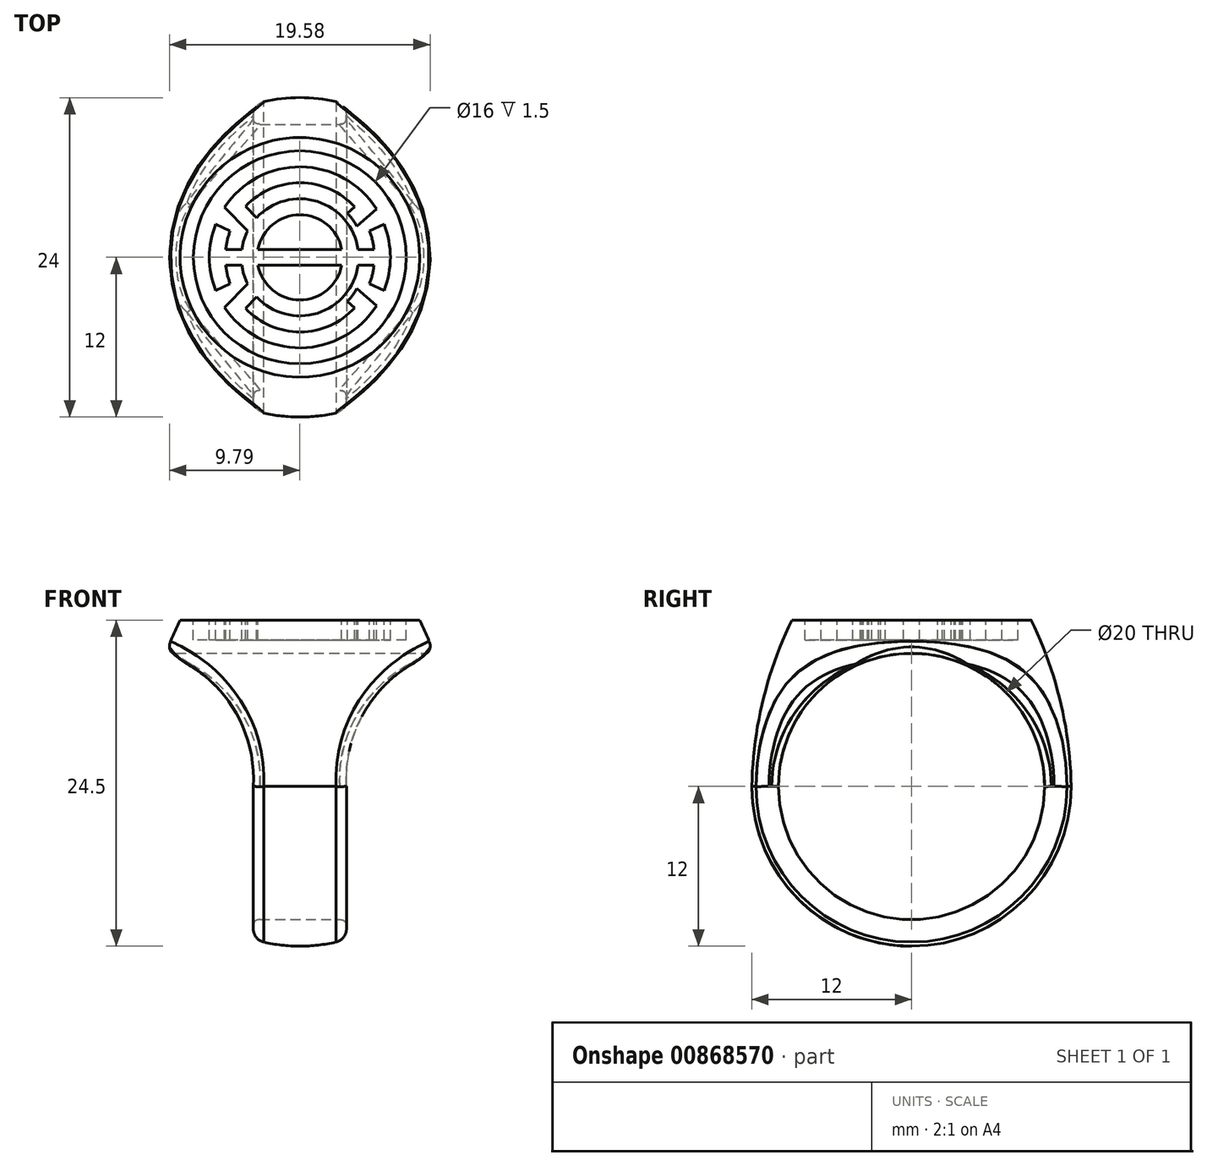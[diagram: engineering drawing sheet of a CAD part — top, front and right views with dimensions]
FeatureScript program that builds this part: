
annotation { "Feature Type Name" : "Feature", "Feature Type Description" : "" }
export const myFeature = defineFeature(function(context is Context, id is Id, definition is map)
    precondition{}
    {
        {
            var Q0;
            Q0=qCreatedBy(makeId("Right.planeOp"),FACE);
            var sketch = newSketch(context, id + "F0", { "sketchPlane" : qUnion([Q0])});
            skLineSegment(sketch, "E0", {"start": v(0, 0) * mm, "end": v(0, -24.5) * mm});
            skLineSegment(sketch, "E1", {"start": v(0, 0) * mm, "end": v(-9, 0) * mm});
            skArc(sketch, "E2", {"start": v(-12, -12.5) * mm, "mid": v(-8.49, -20.99) * mm, "end": v(0, -24.5) * mm});
            skLineSegment(sketch, "E3", {"start": v(0, -12.5) * mm, "end": v(-12, -12.5) * mm, "construction": true});
            skArc(sketch, "E4", {"start": v(-9, 0) * mm, "mid": v(-11.18, -6.09) * mm, "end": v(-12, -12.5) * mm});
            skSolve(sketch);
        }
        {
            var Q0;
            Q0=makeQuery(id+"F0.imprint","IMPRINT",FACE,{"disambiguationData":[TD([[makeQuery(id+"F0.imprint","IMPRINT",EDGE,{"derivedFrom":sQuery(id+"F0.wireOp",EDGE,"E0")}),-1.0]])]});
            var Q1;
            Q1=sQuery(id+"F0.wireOp",EDGE,"E0");
            revolve(context, id + "F1", {"entities" : qUnion([Q0]), "axis" : qUnion([Q1]), "revolveType" : RevolveType.FULL});
        }
        {
            var Q0;
            Q0=qCreatedBy(makeId("Right.planeOp"),FACE);
            var sketch = newSketch(context, id + "F2", { "sketchPlane" : qUnion([Q0])});
            skCircle(sketch, "E5", {"center": v(0, -12.5) * mm, "radius": 10 * mm});
            skSolve(sketch);
        }
        {
            var Q0;
            Q0=qSketchRegion(id+"F2",true);
            extrude(context, id + "F3", {"entities" : qUnion([Q0]), "operationType" : NewBodyOperationType.REMOVE, "endBound" : BoundingType.SYMMETRIC, "oppositeDirection" : true, "depth" : 25 * mm, "offsetDistance" : 25 * mm});
        }
        {
            var Q0;
            Q0=qCreatedBy(makeId("Front.planeOp"),FACE);
            var sketch = newSketch(context, id + "F4", { "sketchPlane" : qUnion([Q0])});
            skLineSegment(sketch, "E6", {"start": v(3.5, -26.5) * mm, "end": v(3.5, -12.5) * mm});
            skArc(sketch, "E7", {"start": v(10.15, -2.5) * mm, "mid": v(5.16, -6.39) * mm, "end": v(3.5, -12.5) * mm});
            skLineSegment(sketch, "E8", {"start": v(10.15, -2.5) * mm, "end": v(11.65, -2.5) * mm});
            skLineSegment(sketch, "E9", {"start": v(11.65, -2.5) * mm, "end": v(11.65, -26.5) * mm});
            skLineSegment(sketch, "E10", {"start": v(11.65, -26.5) * mm, "end": v(3.5, -26.5) * mm});
            skPoint(sketch, "E11.start.orphan", {"position": v(0, -24.5) * mm});
            skLineSegment(sketch, "E12", {"start": v(0, 0) * mm, "end": v(0, -24.5) * mm, "construction": true});
            skLineSegment(sketch, "E13.MirrorCS", {"start": v(-3.5, -26.5) * mm, "end": v(-3.5, -12.5) * mm});
            skArc(sketch, "E14.MirrorCS", {"start": v(-10.15, -2.5) * mm, "mid": v(-5.16, -6.39) * mm, "end": v(-3.5, -12.5) * mm});
            skLineSegment(sketch, "E15.MirrorCS", {"start": v(-11.65, -2.5) * mm, "end": v(-11.65, -26.5) * mm});
            skLineSegment(sketch, "E16.MirrorCS", {"start": v(-11.65, -26.5) * mm, "end": v(-3.5, -26.5) * mm});
            skLineSegment(sketch, "E17.MirrorCS", {"start": v(-10.15, -2.5) * mm, "end": v(-11.65, -2.5) * mm});
            skSolve(sketch);
        }
        {
            var Q0;
            Q0=qSketchRegion(id+"F4",true);
            extrude(context, id + "F5", {"entities" : qUnion([Q0]), "operationType" : NewBodyOperationType.REMOVE, "endBound" : BoundingType.SYMMETRIC, "depth" : 25 * mm, "offsetDistance" : 25 * mm});
        }
        {
            var Q0;
            Q0=makeQuery(id+"F1.opRevolve","SWEPT_FACE",FACE,{"disambiguationData":[OSD([sQuery(id+"F0.wireOp",EDGE,"E1")])]});
            var sketch = newSketch(context, id + "F6", { "sketchPlane" : qUnion([Q0])});
            skCircle(sketch, "E18", {"center": v(0, 0) * mm, "radius": 8 * mm});
            skLineSegment(sketch, "E19", {"start": v(-8, 0) * mm, "end": v(8, 0) * mm, "construction": true});
            skArc(sketch, "E20", {"start": v(3.14, 0.6) * mm, "mid": v(0, 3.2) * mm, "end": v(-3.14, 0.6) * mm});
            skArc(sketch, "E21", {"start": v(4.36, 0.6) * mm, "mid": v(1.32, 4.2) * mm, "end": v(-3.24, 2.98) * mm});
            skArc(sketch, "E22", {"start": v(5.57, 0.6) * mm, "mid": v(5.45, 1.3) * mm, "end": v(5.24, 1.98) * mm});
            skArc(sketch, "E23", {"start": v(6.8, 0) * mm, "mid": v(6.68, 1.26) * mm, "end": v(6.33, 2.49) * mm});
            skLineSegment(sketch, "E24", {"start": v(-4.08, 3.84) * mm, "end": v(-3.24, 2.98) * mm});
            skLineSegment(sketch, "E25", {"start": v(-5.67, 3.75) * mm, "end": v(-3.93, 1.98) * mm});
            skLineSegment(sketch, "E26", {"start": v(-6.33, 2.49) * mm, "end": v(-5.24, 1.98) * mm});
            skArc(sketch, "E27.trimOffspring", {"start": v(-6.33, 2.49) * mm, "mid": v(-6.68, 1.26) * mm, "end": v(-6.8, 0) * mm});
            skArc(sketch, "E28.trimOffspring", {"start": v(-5.24, 1.98) * mm, "mid": v(-5.45, 1.3) * mm, "end": v(-5.57, 0.6) * mm});
            skArc(sketch, "E29.trimOffspring", {"start": v(-3.93, 1.98) * mm, "mid": v(-4.2, 1.3) * mm, "end": v(-4.36, 0.6) * mm});
            skLineSegment(sketch, "E30", {"start": v(-5.57, 0.6) * mm, "end": v(-4.36, 0.6) * mm});
            skLineSegment(sketch, "E31", {"start": v(5.24, 1.98) * mm, "end": v(6.33, 2.49) * mm});
            skLineSegment(sketch, "E32", {"start": v(5.75, 3.62) * mm, "end": v(4.29, 2.33) * mm});
            skLineSegment(sketch, "E33", {"start": v(3.58, 3.3) * mm, "end": v(4.13, 3.79) * mm});
            skLineSegment(sketch, "E34.trimOffspring", {"start": v(4.36, 0.6) * mm, "end": v(5.57, 0.6) * mm});
            skPoint(sketch, "E35.orphan", {"position": v(4.4, 0) * mm});
            skPoint(sketch, "E36.orphan", {"position": v(5.6, 0) * mm});
            skArc(sketch, "E37.trimOffspring", {"start": v(4.13, 3.79) * mm, "mid": v(0.04, 5.6) * mm, "end": v(-4.08, 3.84) * mm});
            skArc(sketch, "E38.trimOffspring", {"start": v(5.75, 3.62) * mm, "mid": v(0.08, 6.8) * mm, "end": v(-5.67, 3.75) * mm});
            skPoint(sketch, "E39.orphan", {"position": v(-5.6, 0) * mm});
            skPoint(sketch, "E40.orphan", {"position": v(-4.4, 0) * mm});
            skLineSegment(sketch, "E41.trimOffspring", {"start": v(-3.14, 0.6) * mm, "end": v(3.14, 0.6) * mm});
            skPoint(sketch, "E42.orphan", {"position": v(-3.2, 0) * mm});
            skArc(sketch, "E43", {"start": v(4.29, 2.33) * mm, "mid": v(3.97, 2.84) * mm, "end": v(3.58, 3.3) * mm});
            skArc(sketch, "E44.MirrorCS", {"start": v(-6.33, -2.49) * mm, "mid": v(-6.68, -1.26) * mm, "end": v(-6.8, 0) * mm});
            skLineSegment(sketch, "E45.MirrorCS", {"start": v(-6.33, -2.49) * mm, "end": v(-5.24, -1.98) * mm});
            skArc(sketch, "E46.MirrorCS", {"start": v(-5.24, -1.98) * mm, "mid": v(-5.45, -1.3) * mm, "end": v(-5.57, -0.6) * mm});
            skLineSegment(sketch, "E47.MirrorCS", {"start": v(-5.57, -0.6) * mm, "end": v(-4.36, -0.6) * mm});
            skArc(sketch, "E48.MirrorCS", {"start": v(-3.93, -1.98) * mm, "mid": v(-4.2, -1.3) * mm, "end": v(-4.36, -0.6) * mm});
            skLineSegment(sketch, "E49.MirrorCS", {"start": v(-5.67, -3.75) * mm, "end": v(-3.93, -1.98) * mm});
            skArc(sketch, "E50.MirrorCS", {"start": v(5.75, -3.62) * mm, "mid": v(0.08, -6.8) * mm, "end": v(-5.67, -3.75) * mm});
            skLineSegment(sketch, "E51.MirrorCS", {"start": v(5.75, -3.62) * mm, "end": v(4.29, -2.33) * mm});
            skArc(sketch, "E52.MirrorCS", {"start": v(4.29, -2.33) * mm, "mid": v(3.97, -2.84) * mm, "end": v(3.58, -3.3) * mm});
            skArc(sketch, "E53.MirrorCS", {"start": v(4.13, -3.79) * mm, "mid": v(0.04, -5.6) * mm, "end": v(-4.08, -3.84) * mm});
            skLineSegment(sketch, "E54.MirrorCS", {"start": v(-4.08, -3.84) * mm, "end": v(-3.24, -2.98) * mm});
            skArc(sketch, "E55.MirrorCS", {"start": v(4.36, -0.6) * mm, "mid": v(1.32, -4.2) * mm, "end": v(-3.24, -2.98) * mm});
            skLineSegment(sketch, "E56.MirrorCS", {"start": v(4.36, -0.6) * mm, "end": v(5.57, -0.6) * mm});
            skArc(sketch, "E57.MirrorCS", {"start": v(5.57, -0.6) * mm, "mid": v(5.45, -1.3) * mm, "end": v(5.24, -1.98) * mm});
            skLineSegment(sketch, "E58.MirrorCS", {"start": v(5.24, -1.98) * mm, "end": v(6.33, -2.49) * mm});
            skArc(sketch, "E59.MirrorCS", {"start": v(6.8, 0) * mm, "mid": v(6.68, -1.26) * mm, "end": v(6.33, -2.49) * mm});
            skLineSegment(sketch, "E60.MirrorCS", {"start": v(-3.14, -0.6) * mm, "end": v(3.14, -0.6) * mm});
            skArc(sketch, "E61.MirrorCS", {"start": v(3.14, -0.6) * mm, "mid": v(0, -3.2) * mm, "end": v(-3.14, -0.6) * mm});
            skLineSegment(sketch, "E62.MirrorCS", {"start": v(3.58, -3.3) * mm, "end": v(4.13, -3.79) * mm});
            skSolve(sketch);
        }
        {
            var Q0;
            Q0=makeQuery(id+"F6.imprint","IMPRINT",FACE,{"disambiguationData":[TD([[makeQuery(id+"F6.imprint","IMPRINT",EDGE,{"derivedFrom":sQuery(id+"F6.wireOp",EDGE,"E18")}),1.0]])]});
            var Q1;
            Q1=makeQuery(id+"F6.imprint","IMPRINT",FACE,{"disambiguationData":[TD([[makeQuery(id+"F6.imprint","IMPRINT",EDGE,{"derivedFrom":sQuery(id+"F6.wireOp",EDGE,"E20")}),1.0]])]});
            var Q2;
            Q2=makeQuery(id+"F6.imprint","IMPRINT",FACE,{"disambiguationData":[TD([[makeQuery(id+"F6.imprint","IMPRINT",EDGE,{"derivedFrom":sQuery(id+"F6.wireOp",EDGE,"E60.MirrorCS")}),-1.0]])]});
            extrude(context, id + "F7", {"entities" : qUnion([Q0, Q1, Q2]), "operationType" : NewBodyOperationType.REMOVE, "oppositeDirection" : true, "depth" : 1.5 * mm, "offsetDistance" : 25 * mm});
        }
        {
            var Q0;
            Q0=makeQuery(id+"F5.boolean.opBoolean","INTERSECT",EDGE,{"disambiguationData":[OD(1.0)],"derivedFrom":[makeQuery(id+"F1.opRevolve","SWEPT_FACE",FACE,{"disambiguationData":[OSD([sQuery(id+"F0.wireOp",EDGE,"E4")])]}),makeQuery(id+"F5.opExtrude","SWEPT_FACE",FACE,{"disambiguationData":[OSD([sQuery(id+"F4.wireOp",EDGE,"E14.MirrorCS")])]})]});
            var Q1;
            Q1=makeQuery(id+"F5.boolean.opBoolean","INTERSECT",EDGE,{"derivedFrom":[makeQuery(id+"F1.opRevolve","SWEPT_FACE",FACE,{"disambiguationData":[OSD([sQuery(id+"F0.wireOp",EDGE,"E2")])]}),makeQuery(id+"F5.opExtrude","SWEPT_FACE",FACE,{"disambiguationData":[OSD([sQuery(id+"F4.wireOp",EDGE,"E13.MirrorCS")])]})]});
            var Q2;
            Q2=makeQuery(id+"F5.boolean.opBoolean","INTERSECT",EDGE,{"disambiguationData":[OD(1.0)],"derivedFrom":[makeQuery(id+"F1.opRevolve","SWEPT_FACE",FACE,{"disambiguationData":[OSD([sQuery(id+"F0.wireOp",EDGE,"E4")])]}),makeQuery(id+"F5.opExtrude","SWEPT_FACE",FACE,{"disambiguationData":[OSD([sQuery(id+"F4.wireOp",EDGE,"E7")])]})]});
            var Q3;
            Q3=makeQuery(id+"F5.boolean.opBoolean","INTERSECT",EDGE,{"derivedFrom":[makeQuery(id+"F1.opRevolve","SWEPT_FACE",FACE,{"disambiguationData":[OSD([sQuery(id+"F0.wireOp",EDGE,"E2")])]}),makeQuery(id+"F5.opExtrude","SWEPT_FACE",FACE,{"disambiguationData":[OSD([sQuery(id+"F4.wireOp",EDGE,"E6")])]})]});
            fillet(context, id + "F8", {"entities" : qUnion([Q0, Q1, Q2, Q3]), "radius" : 1 * mm, "allowEdgeOverflow" : false});
        }
        {
            var Q0;
            Q0=makeQuery(id+"F5.boolean.opBoolean","INTERSECT",EDGE,{"disambiguationData":[OD(1.0)],"derivedFrom":[makeQuery(id+"F3.boolean.opBoolean","COPY",FACE,{"derivedFrom":makeQuery(id+"F3.opExtrude","SWEPT_FACE",FACE,{"disambiguationData":[OSD([sQuery(id+"F2.wireOp",EDGE,"E5")])]})}),makeQuery(id+"F5.opExtrude","SWEPT_FACE",FACE,{"disambiguationData":[OSD([sQuery(id+"F4.wireOp",EDGE,"E14.MirrorCS")])]})]});
            var Q1;
            Q1=makeQuery(id+"F5.boolean.opBoolean","INTERSECT",EDGE,{"derivedFrom":[makeQuery(id+"F3.boolean.opBoolean","COPY",FACE,{"derivedFrom":makeQuery(id+"F3.opExtrude","SWEPT_FACE",FACE,{"disambiguationData":[OSD([sQuery(id+"F2.wireOp",EDGE,"E5")])]})}),makeQuery(id+"F5.opExtrude","SWEPT_FACE",FACE,{"disambiguationData":[OSD([sQuery(id+"F4.wireOp",EDGE,"E13.MirrorCS")])]})]});
            var Q2;
            Q2=makeQuery(id+"F5.boolean.opBoolean","INTERSECT",EDGE,{"disambiguationData":[OD(0.0)],"derivedFrom":[makeQuery(id+"F3.boolean.opBoolean","COPY",FACE,{"derivedFrom":makeQuery(id+"F3.opExtrude","SWEPT_FACE",FACE,{"disambiguationData":[OSD([sQuery(id+"F2.wireOp",EDGE,"E5")])]})}),makeQuery(id+"F5.opExtrude","SWEPT_FACE",FACE,{"disambiguationData":[OSD([sQuery(id+"F4.wireOp",EDGE,"E14.MirrorCS")])]})]});
            var Q3;
            Q3=makeQuery(id+"F5.boolean.opBoolean","INTERSECT",EDGE,{"disambiguationData":[OD(0.0)],"derivedFrom":[makeQuery(id+"F3.boolean.opBoolean","COPY",FACE,{"derivedFrom":makeQuery(id+"F3.opExtrude","SWEPT_FACE",FACE,{"disambiguationData":[OSD([sQuery(id+"F2.wireOp",EDGE,"E5")])]})}),makeQuery(id+"F5.opExtrude","SWEPT_FACE",FACE,{"disambiguationData":[OSD([sQuery(id+"F4.wireOp",EDGE,"E7")])]})]});
            var Q4;
            Q4=makeQuery(id+"F3.boolean.opBoolean","COPY",FACE,{"derivedFrom":makeQuery(id+"F3.opExtrude","SWEPT_FACE",FACE,{"disambiguationData":[OSD([sQuery(id+"F2.wireOp",EDGE,"E5")])]})});
            fillet(context, id + "F9", {"entities" : qUnion([Q0, Q1, Q2, Q3, Q4]), "radius" : .5 * mm, "rho" : 0.5, "crossSection" : FilletCrossSection.CONIC, "allowEdgeOverflow" : false});
        }
    });
